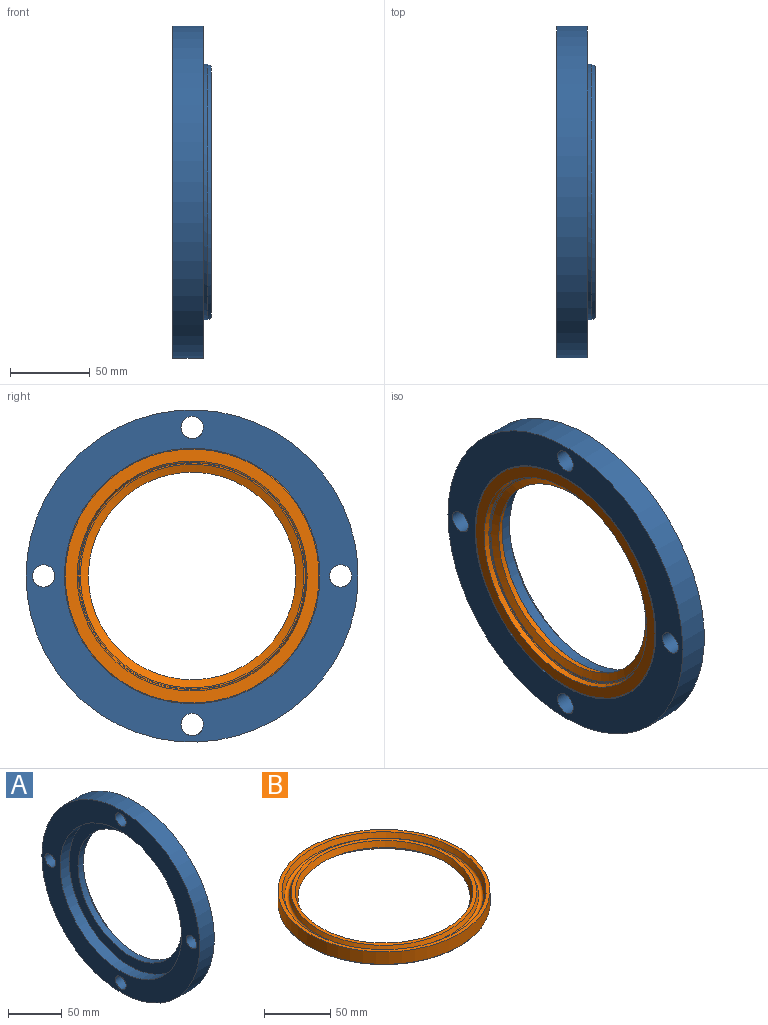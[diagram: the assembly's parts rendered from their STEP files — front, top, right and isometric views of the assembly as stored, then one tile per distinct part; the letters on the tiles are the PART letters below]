
ASSEMBLY  parts=2 mates=1
PART A: 15 faces, bbox 27.6x208x208 mm
  f0: cylinder r=68.5mm len=137mm, axis (1,0,0), area 3012.8mm2, adj f1,f7
  f1: plane 139x139mm, normal (1,0,0), area 433.5mm2, adj f0,f10
  f2: cylinder r=104mm len=208mm, axis (1,0,0), area 12415.6mm2, adj f3,f4
  f3: plane 208x208mm, normal (-1,0,0), area 13257.5mm2, adj f2,f8,f11,f12,f13,f14
  f4: plane 208x208mm, normal (1,0,0), area 13257.5mm2, adj f2,f5,f11,f12,f13,f14
  f5: cylinder r=80mm len=160mm, axis (-1,0,0), area 1508mm2, adj f4,f9
  f6: plane 157.69x157.69mm, normal (1,0,0), area 2093.3mm2, adj f9,f10
  f7: plane 160x160mm, normal (-1,0,0), area 5365.1mm2, adj f0,f8
  f8: cylinder r=80mm len=160mm, axis (-1,0,0), area 6031.9mm2, adj f3,f7
  f9: cone r=78.85mm half-angle=30deg, axis (-1,0,0), area 1152.5mm2, adj f5,f6
  f10: torus R=69.5mm, axis (1,0,0), area 3586.8mm2, adj f1,f6
  f11: cylinder r=7mm len=19mm, axis (-1,0,0), area 835.7mm2, adj f3,f4
  f12: cylinder r=7mm len=19mm, axis (-1,0,0), area 835.7mm2, adj f3,f4
  f13: cylinder r=7mm len=19mm, axis (-1,0,0), area 835.7mm2, adj f3,f4
  f14: cylinder r=7mm len=19mm, axis (-1,0,0), area 835.7mm2, adj f3,f4
PART B: 13 faces, bbox 173.2x173.2x12 mm
  f0: cone r=77mm half-angle=22.5deg, axis (0,0,1), area 2322.3mm2, adj f1,f10
  f1: plane 160x160mm, normal (0,0,1), area 1479.7mm2, adj f0,f2
  f2: cylinder r=80mm len=160mm, axis (0,0,1), area 5780.5mm2, adj f1,f12
  f3: plane 159x159mm, normal (0,0,-1), area 3569.6mm2, adj f4,f12
  f4: cone r=71.29mm half-angle=10deg, axis (0,0,-1), area 1640.4mm2, adj f3,f11
  f5: plane 141.75x141.75mm, normal (0,0,-1), area 387.3mm2, adj f6,f11
  f6: cone r=65mm half-angle=68.2deg, axis (0,0,-1), area 2283.9mm2, adj f5,f7
  f7: cone r=67mm half-angle=21.8deg, axis (0,0,1), area 2233.2mm2, adj f6,f8
  f8: plane 140x140mm, normal (0,0,1), area 1291.2mm2, adj f7,f9
  f9: cone r=71.45mm half-angle=22.5deg, axis (0,0,-1), area 1678.1mm2, adj f8,f10
  f10: torus R=73.29mm, axis (0,0,1), area 2170.1mm2, adj f0,f9
  f11: torus R=70.88mm, axis (0,0,1), area 312.2mm2, adj f4,f5
  f12: torus R=79.5mm, axis (0,0,1), area 393.9mm2, adj f2,f3
PLACE A at identity fixed
PLACE B rot(axis=(0.71,0,0.71),180deg) t=(-19,0,0)mm
MATE fastened B.f0 <-> A.f0  axis (-1,0,0) through (-19,0,0)mm
